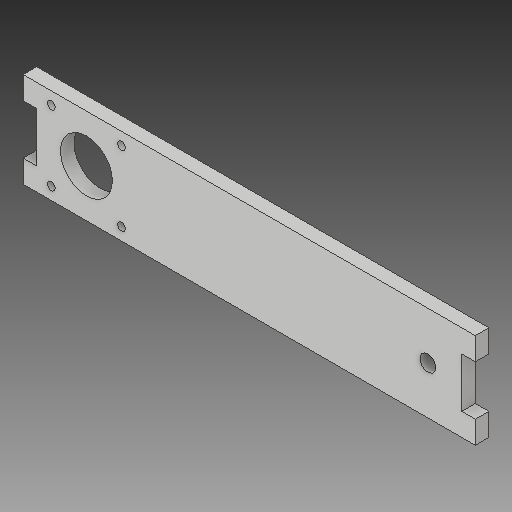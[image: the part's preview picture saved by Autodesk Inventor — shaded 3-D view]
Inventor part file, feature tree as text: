
AUTODESK INVENTOR PART (.ipt)
format: ipt  version: 2019 (Build 230136000, 136)  size: 135,168 bytes
history: native  units: mm
features: extrude x1, sketch x1
ambient origin geometry x8: Origin, YZ Plane, XZ Plane, XY Plane, X Axis, Y Axis, Z Axis, Center Point
bodies: Body1 (feature_tree)
feature tree (2):
  extrude  "Extrusion2"  Depth=3.5mm
  sketch  "Sketch1"  dims[d13=3.5mm d14=3.5mm d15=15.5mm d16=15.5mm d21=3.5mm d22=3.5mm d23=31.0mm d24=23.0mm d25=6.0mm d26=0.0mm d29=21.0mm d30=15.5mm d31=200.0mm d32=21.0mm d34=21.0mm d35=6.0mm d36=10.0mm d37=10.0mm d38=28.0mm d39=10.0mm d40=10.0mm d41=6.0mm d42=7.0mm d43=15.0mm d44=21.0mm]
